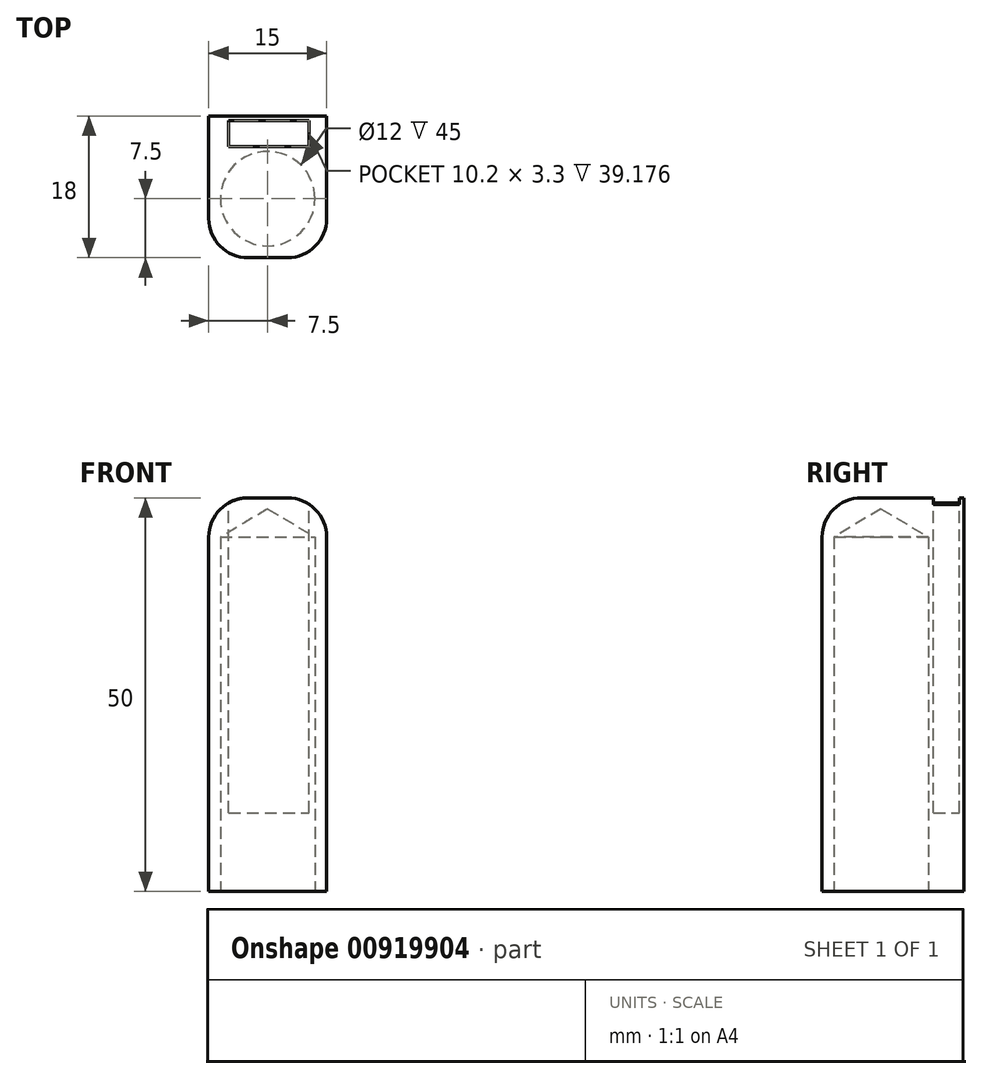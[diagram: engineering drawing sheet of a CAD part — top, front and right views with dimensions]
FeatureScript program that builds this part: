
annotation { "Feature Type Name" : "Feature", "Feature Type Description" : "" }
export const myFeature = defineFeature(function(context is Context, id is Id, definition is map)
    precondition{}
    {
        {
            var Q0;
            Q0=qCreatedBy(makeId("Top.planeOp"),FACE);
            var sketch = newSketch(context, id + "F0", { "sketchPlane" : qUnion([Q0])});
            skLineSegment(sketch, "E0.bottom", {"start": v(-7.5, -7.5) * mm, "end": v(7.5, -7.5) * mm});
            skLineSegment(sketch, "E0.top", {"start": v(-7.5, 10.5) * mm, "end": v(7.5, 10.5) * mm});
            skLineSegment(sketch, "E0.left", {"start": v(-7.5, -7.5) * mm, "end": v(-7.5, 10.5) * mm});
            skLineSegment(sketch, "E0.right", {"start": v(7.5, -7.5) * mm, "end": v(7.5, 10.5) * mm});
            skCircle(sketch, "E1", {"center": v(0, 0) * mm, "radius": 6 * mm});
            skLineSegment(sketch, "E2.bottom", {"start": v(-5.25, 9.95) * mm, "end": v(4.95, 9.95) * mm});
            skLineSegment(sketch, "E2.top", {"start": v(-5.25, 6.65) * mm, "end": v(4.95, 6.65) * mm});
            skLineSegment(sketch, "E2.left", {"start": v(-5.25, 9.95) * mm, "end": v(-5.25, 6.65) * mm});
            skLineSegment(sketch, "E2.right", {"start": v(4.95, 9.95) * mm, "end": v(4.95, 6.65) * mm});
            skSolve(sketch);
        }
        {
            var Q0;
            Q0=makeQuery(id+"F0.imprint","IMPRINT",FACE,{"disambiguationData":[TD([[makeQuery(id+"F0.imprint","IMPRINT",EDGE,{"derivedFrom":sQuery(id+"F0.wireOp",EDGE,"E0.bottom")}),1.0]])]});
            var Q1;
            Q1=makeQuery(id+"F0.imprint","IMPRINT",FACE,{"disambiguationData":[TD([[makeQuery(id+"F0.imprint","IMPRINT",EDGE,{"derivedFrom":sQuery(id+"F0.wireOp",EDGE,"E2.bottom")}),-1.0]])]});
            var Q2;
            Q2=makeQuery(id+"F0.imprint","IMPRINT",FACE,{"disambiguationData":[TD([[makeQuery(id+"F0.imprint","IMPRINT",EDGE,{"derivedFrom":sQuery(id+"F0.wireOp",EDGE,"E1")}),1.0]])]});
            extrude(context, id + "F1", {"entities" : qUnion([Q0, Q1, Q2]), "depth" : 50 * mm, "offsetDistance" : 25 * mm});
        }
        {
            var Q0;
            Q0=sQuery(id+"F0.wireOp",VERTEX,"E1.center");
            var Q1;
            Q1=makeQuery(id+"F1.opExtrude","SWEPT_BODY",BODY,{"disambiguationData":[OSD([sQuery(id+"F0.wireOp",EDGE,"E0.bottom"),sQuery(id+"F0.wireOp",EDGE,"E0.top"),sQuery(id+"F0.wireOp",EDGE,"E0.left"),sQuery(id+"F0.wireOp",EDGE,"E0.right")])]});
            hole(context, id + "F2", {"style" : HoleStyle.SIMPLE, "endStyle" : HoleEndStyle.BLIND, "oppositeDirection" : true, "holeDiameter" : 12 * mm, "majorDiameter" : 5 * mm, "holeDepth" : 45 * mm, "isTappedThrough" : true, "tappedDepth" : 12 * mm, "tapClearance" : 3, "locations" : qUnion([Q0]), "scope" : qUnion([Q1])});
        }
        {
            var Q0;
            Q0=makeQuery(id+"F1.opExtrude","SWEPT_EDGE",EDGE,{"disambiguationData":[OSD([sQuery(id+"F0.wireOp",EDGE,"E0.bottom"),sQuery(id+"F0.wireOp",EDGE,"E0.right")])]});
            var Q1;
            Q1=makeQuery(id+"F1.opExtrude","SWEPT_EDGE",EDGE,{"disambiguationData":[OSD([sQuery(id+"F0.wireOp",EDGE,"E0.bottom"),sQuery(id+"F0.wireOp",EDGE,"E0.left")])]});
            fillet(context, id + "F3", {"entities" : qUnion([Q0, Q1]), "radius" : 5 * mm, "tangentPropagation" : true, "allowEdgeOverflow" : false});
        }
        {
            var Q0;
            Q0=makeQuery(id+"F1.opExtrude","CAP_EDGE",EDGE,{"disambiguationData":[OSD([sQuery(id+"F0.wireOp",EDGE,"E0.left")])],"isStart":false});
            fillet(context, id + "F4", {"entities" : qUnion([Q0]), "radius" : 5 * mm, "tangentPropagation" : true, "allowEdgeOverflow" : false});
        }
        {
            var Q0;
            Q0=qCreatedBy(makeId("Top.planeOp"),FACE);
            cPlane(context, id + "F5", {"entities" : qUnion([Q0]), "cplaneType" : CPlaneType.OFFSET, "offset" : 50 * mm, "width" : 150 * mm, "height" : 150 * mm});
        }
        {
            var Q0;
            Q0=qCreatedBy(id+"F5.planeOp",FACE);
            var sketch = newSketch(context, id + "F6", { "sketchPlane" : qUnion([Q0])});
            skLineSegment(sketch, "E3.bottom", {"start": v(-4.95, 6.65) * mm, "end": v(5.25, 6.65) * mm});
            skLineSegment(sketch, "E3.top", {"start": v(-4.95, 9.95) * mm, "end": v(5.25, 9.95) * mm});
            skLineSegment(sketch, "E3.left", {"start": v(-4.95, 6.65) * mm, "end": v(-4.95, 9.95) * mm});
            skLineSegment(sketch, "E3.right", {"start": v(5.25, 6.65) * mm, "end": v(5.25, 9.95) * mm});
            skSolve(sketch);
        }
        {
            var Q0;
            Q0 = qSketchRegion(id + "F6", true);
            extrude(context, id + "F7", {"entities" : qUnion([Q0]), "operationType" : NewBodyOperationType.REMOVE, "oppositeDirection" : true, "depth" : 40 * mm, "offsetDistance" : 25 * mm});
        }
    });
